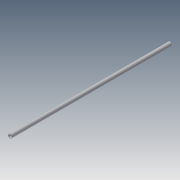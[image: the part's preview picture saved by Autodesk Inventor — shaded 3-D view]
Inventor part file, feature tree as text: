
AUTODESK INVENTOR PART (.ipt)
format: ipt  version: 2013 SP2 (Build 170200200, 200)  size: 126,976 bytes
history: native  units: in
note: dims shown in document units (in); Inventor stores cm internally (conversion verified against a paired STEP export)
features: extrude x1, sketch x1
ambient origin geometry x8: Origin, YZ Plane, XZ Plane, XY Plane, X Axis, Y Axis, Z Axis, Center Point
bodies: Solid1 (feature_tree)
feature tree (2):
  extrude  "Extrusion1"  Depth=0.154in
  sketch  "Sketch1"  dims[d0=2.375in d2=0.154in d3=96.0in d4=0.0in]
